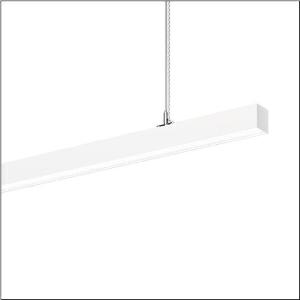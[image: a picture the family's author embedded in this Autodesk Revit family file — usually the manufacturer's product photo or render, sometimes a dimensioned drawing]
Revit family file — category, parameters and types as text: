
# Revit family: silica_r__21_51mx30db35wb_0444
name_source: partatom
category: Lighting Fixtures
units: mm (PartAtom-declared; Revit-internal decimal feet)

## family parameters
Cut with Voids When Loaded = No
Host = Face
Light Source = No
Part Type = Normal
Room Calculation Point = No
Round Connector Dimension = Use Diameter
Shared = No

## types (1)
- --- (1 x LED, 5260 lm, 34.1 W, 3000K)
    Apparent Load = 34 VA
    CIE Flux Codes = 47 79 96 57 100
    Color Rendering = 80
    Color Temperature = 3000K
    Default Elevation = 1800 mm
    Description = Silica® 21, office luminaire, primary optical cover: cover, of PMMA, opal, light emission: direct/indirect distribution, primary light characteristic: symmetric, installation type: suspended mounting, LED, rated luminous flux: 5.260lm, luminous efficacy: 154lm/W, light colour: 830, colour temperature: 3000K, with terminal, 3+2-pole, max. 2.5mm², mains connection: 220..240V, AC, 50/60Hz, rated input power: 34.1W, luminaire housing, of aluminium, traffic white (RAL 9016), length: 1.504mm, width: 53mm, height: 53mm, protection rating (complete): IP20, insulation class (complete): insulation class I (protective earthing), certification: CE, permissible operating ambient temperature: 0..+35°C, standard: EN 50419, packaging unit: 1 piece
    Height = 53 mm
    Lamp = 1 x LED
    Lamp Light Flux = 5260 lm
    Lamp Power = 34.1 W
    Lamp count = 1
    Length = 1504 mm
    Luminous efficacy = 154 lm/W
    Manufacturer = Siteco
    ModVariant = No
    Model = 51MX30DB35WB
    Mounting Place = Ceiling
    Mounting Type = Pendant
    Number of Poles = 1
    OnlyDefault = Yes
    Power Factor = 1
    Product Name = Silica® 21
    Product group = office luminaire | ceiling pendant
    ProductGroupID = 902
    Protection Class = Protection class I
    Protection Degree = IP 20
    RLX_Detail_Level = 1
    RLX_Emergency_Light_Flux = 0 lm
    RLX_Emergency_Type = 0
    RLX_Emergency_Type_DB = No
    RlxData = <blob elided: 21481 chars, md5=a432ab5c>
    Socket = socket
    Standby Power = 0 W
    System Light Flux = 5260 lm
    System Power = 34 W
    Type Comments = factory setting: luminous flux: 100 % | dim-lin: 254 | 233 mA
    Type Image = l_1313629.jpg
    URL = http://relux.com
    VarID = @adj_065049
    Voltage = 0 V
    Weight = 0.00 kg
    Width = 53 mm

## geometry (parser evidence)
native form markers: Blend x4, Sweep x13
no freeform markers — native parametric forms only
